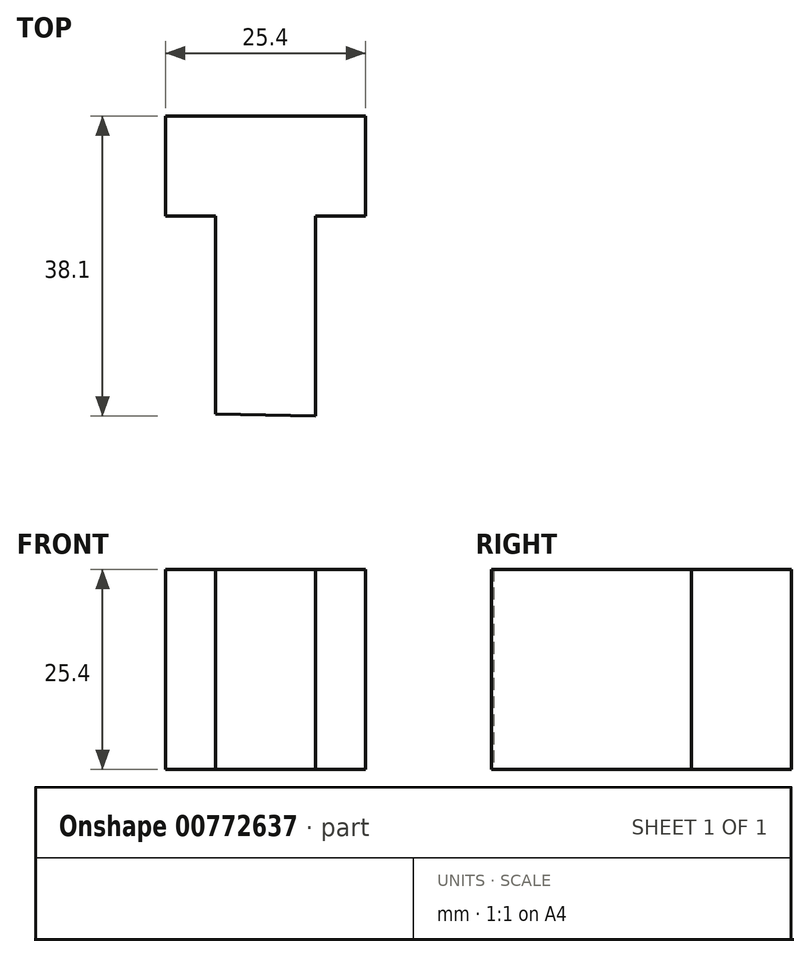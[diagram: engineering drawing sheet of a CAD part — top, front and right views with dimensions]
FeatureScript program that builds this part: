
annotation { "Feature Type Name" : "Feature", "Feature Type Description" : "" }
export const myFeature = defineFeature(function(context is Context, id is Id, definition is map)
    precondition{}
    {
        {
            var Q0;
            Q0=qCreatedBy(makeId("Top.planeOp"),FACE);
            var sketch = newSketch(context, id + "F0", { "sketchPlane" : qUnion([Q0])});
            skLineSegment(sketch, "E0", {"start": v(0, 49.14) * mm, "end": v(25.4, 49.14) * mm});
            skLineSegment(sketch, "E1", {"start": v(25.4, 49.14) * mm, "end": v(25.4, 36.44) * mm});
            skLineSegment(sketch, "E2", {"start": v(0, 49.14) * mm, "end": v(0, 36.44) * mm});
            skLineSegment(sketch, "E3", {"start": v(0, 36.44) * mm, "end": v(6.36, 36.44) * mm});
            skLineSegment(sketch, "E4", {"start": v(25.4, 36.44) * mm, "end": v(19.05, 36.44) * mm});
            skLineSegment(sketch, "E5", {"start": v(6.36, 36.44) * mm, "end": v(6.36, 11.04) * mm});
            skLineSegment(sketch, "E6", {"start": v(19.05, 36.44) * mm, "end": v(19.05, 11.04) * mm});
            skLineSegment(sketch, "E7", {"start": v(6.36, 11.32) * mm, "end": v(19.05, 11.04) * mm});
            skSolve(sketch);
        }
        {
            var Q0;
            Q0 = qSketchRegion(id + "F0", true);
            extrude(context, id + "F1", {"entities" : qUnion([Q0]), "depth" : 25.4 * mm, "offsetDistance" : 25.4 * mm});
        }
    });
